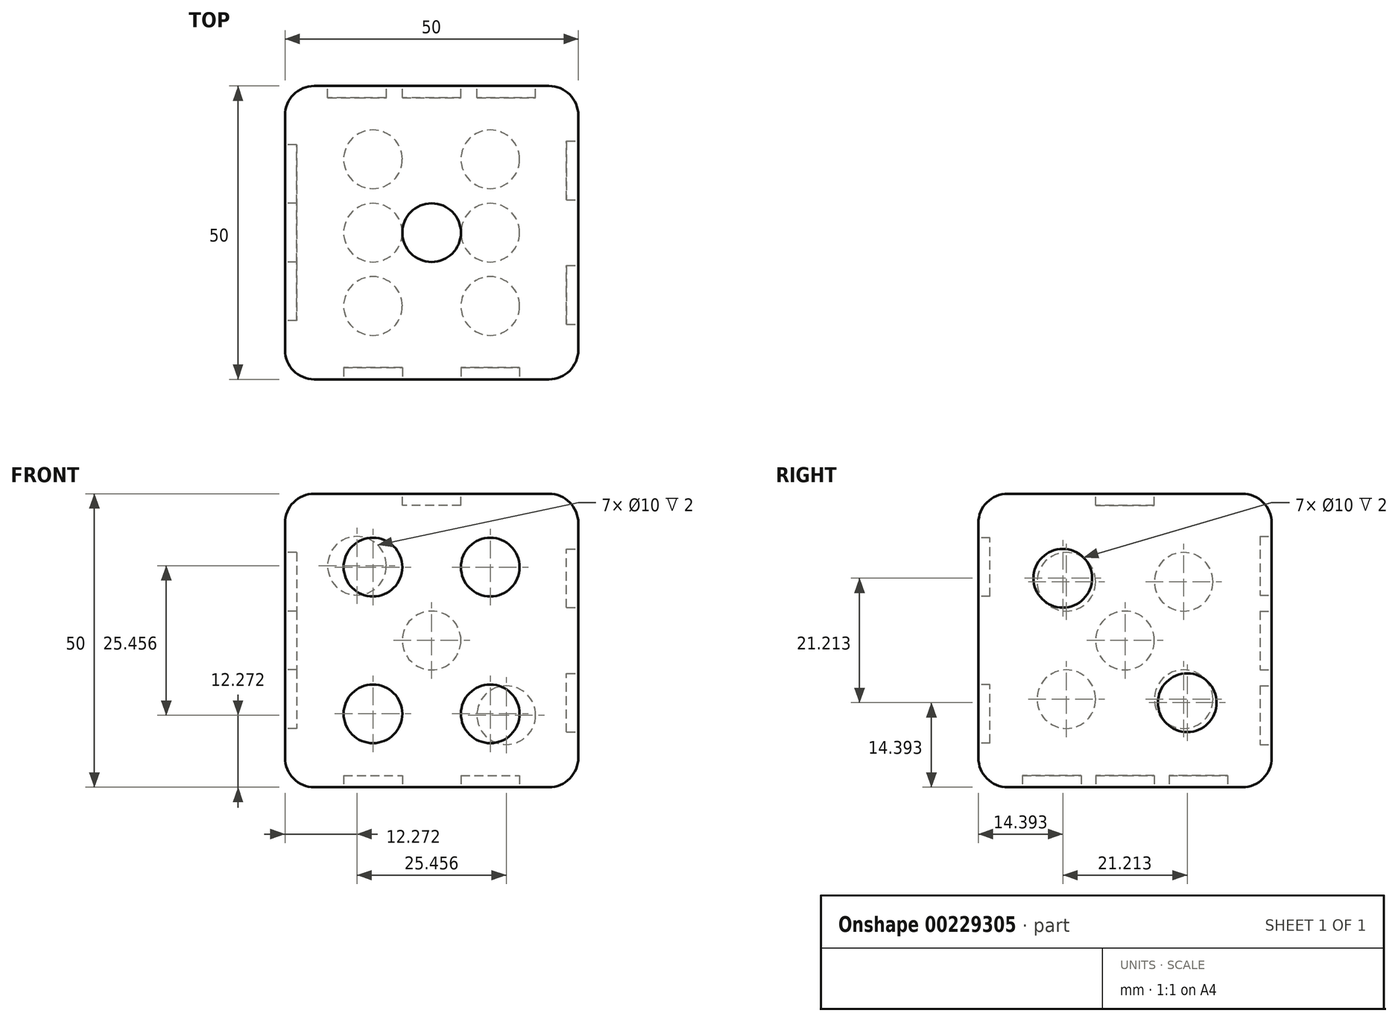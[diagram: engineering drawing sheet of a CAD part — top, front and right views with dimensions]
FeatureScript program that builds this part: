
annotation { "Feature Type Name" : "Feature", "Feature Type Description" : "" }
export const myFeature = defineFeature(function(context is Context, id is Id, definition is map)
    precondition{}
    {
        {
            var Q0;
            Q0=qCreatedBy(makeId("Top.planeOp"),FACE);
            var sketch = newSketch(context, id + "F0", { "sketchPlane" : qUnion([Q0])});
            skLineSegment(sketch, "E0.bottom", {"start": v(-25, 25) * mm, "end": v(25, 25) * mm});
            skLineSegment(sketch, "E0.top", {"start": v(-25, -25) * mm, "end": v(25, -25) * mm});
            skLineSegment(sketch, "E0.left", {"start": v(-25, 25) * mm, "end": v(-25, -25) * mm});
            skLineSegment(sketch, "E0.right", {"start": v(25, 25) * mm, "end": v(25, -25) * mm});
            skPoint(sketch, "E1", {"position": v(0, 25) * mm});
            skPoint(sketch, "E2", {"position": v(25, 0) * mm});
            skSolve(sketch);
        }
        {
            var Q0;
            Q0=makeQuery(id+"F0.imprint","IMPRINT",FACE,{"disambiguationData":[TD([[makeQuery(id+"F0.imprint","IMPRINT",EDGE,{"derivedFrom":sQuery(id+"F0.wireOp",EDGE,"E0.bottom")}),-1.0]])]});
            extrude(context, id + "F1", {"entities" : qUnion([Q0]), "depth" : 50 * mm});
        }
        {
            var Q0;
            Q0=makeQuery(id+"F1.opExtrude","CAP_FACE",FACE,{"disambiguationData":[OSD([sQuery(id+"F0.wireOp",EDGE,"E0.bottom"),sQuery(id+"F0.wireOp",EDGE,"E0.top"),sQuery(id+"F0.wireOp",EDGE,"E0.left"),sQuery(id+"F0.wireOp",EDGE,"E0.right")])],"isStart":false});
            var sketch = newSketch(context, id + "F2", { "sketchPlane" : qUnion([Q0])});
            skCircle(sketch, "E3", {"center": v(0, 0) * mm, "radius": 5 * mm});
            skSolve(sketch);
        }
        {
            var Q0;
            Q0=makeQuery(id+"F2.imprint","IMPRINT",FACE,{"disambiguationData":[TD([[makeQuery(id+"F2.imprint","IMPRINT",EDGE,{"derivedFrom":sQuery(id+"F2.wireOp",EDGE,"E3")}),1.0]])]});
            extrude(context, id + "F3", {"entities" : qUnion([Q0]), "operationType" : NewBodyOperationType.REMOVE, "oppositeDirection" : true, "depth" : 2 * mm});
        }
        {
            var Q0;
            Q0=makeQuery(id+"F1.opExtrude","SWEPT_FACE",FACE,{"disambiguationData":[OSD([sQuery(id+"F0.wireOp",EDGE,"E0.right")])]});
            var sketch = newSketch(context, id + "F4", { "sketchPlane" : qUnion([Q0])});
            skCircle(sketch, "E4", {"center": v(-10.6, 35.6) * mm, "radius": 5 * mm});
            skCircle(sketch, "E5", {"center": v(10.6, 14.4) * mm, "radius": 5 * mm});
            skLineSegment(sketch, "E6", {"start": v(-25, 50) * mm, "end": v(25, 0) * mm, "construction": true});
            skLineSegment(sketch, "E7", {"start": v(-10.6, 35.6) * mm, "end": v(10.6, 14.4) * mm, "construction": true});
            skPoint(sketch, "E8", {"position": v(0, 25) * mm});
            skSolve(sketch);
        }
        {
            var Q0;
            Q0=makeQuery(id+"F4.imprint","IMPRINT",FACE,{"disambiguationData":[TD([[makeQuery(id+"F4.imprint","IMPRINT",EDGE,{"derivedFrom":sQuery(id+"F4.wireOp",EDGE,"E5")}),1.0]])]});
            var Q1;
            Q1=makeQuery(id+"F4.imprint","IMPRINT",FACE,{"disambiguationData":[TD([[makeQuery(id+"F4.imprint","IMPRINT",EDGE,{"derivedFrom":sQuery(id+"F4.wireOp",EDGE,"E4")}),1.0]])]});
            var Q2;
            Q2=sQuery(id+"F4.wireOp",EDGE,"E4");
            var Q3;
            Q3=sQuery(id+"F4.wireOp",EDGE,"E5");
            extrude(context, id + "F5", {"entities" : qUnion([Q0, Q1]), "operationType" : NewBodyOperationType.REMOVE, "surfaceEntities" : qUnion([Q2, Q3]), "oppositeDirection" : true, "depth" : 2 * mm});
        }
        {
            var Q0;
            Q0=makeQuery(id+"F1.opExtrude","CAP_FACE",FACE,{"disambiguationData":[OSD([sQuery(id+"F0.wireOp",EDGE,"E0.bottom"),sQuery(id+"F0.wireOp",EDGE,"E0.top"),sQuery(id+"F0.wireOp",EDGE,"E0.left"),sQuery(id+"F0.wireOp",EDGE,"E0.right")])],"isStart":true});
            var sketch = newSketch(context, id + "F6", { "sketchPlane" : qUnion([Q0])});
            skCircle(sketch, "E9", {"center": v(10, 12.5) * mm, "radius": 5 * mm});
            skCircle(sketch, "E10", {"center": v(10, 0) * mm, "radius": 5 * mm});
            skCircle(sketch, "E11", {"center": v(10, -12.5) * mm, "radius": 5 * mm});
            skCircle(sketch, "E12", {"center": v(-10, 12.5) * mm, "radius": 5 * mm});
            skCircle(sketch, "E13", {"center": v(-10, 0) * mm, "radius": 5 * mm});
            skCircle(sketch, "E14", {"center": v(-10, -12.5) * mm, "radius": 5 * mm});
            skLineSegment(sketch, "E15", {"start": v(-10, 0) * mm, "end": v(10, 0) * mm, "construction": true});
            skPoint(sketch, "E16", {"position": v(0, 0) * mm});
            skLineSegment(sketch, "E17", {"start": v(-10, 12.5) * mm, "end": v(-10, -12.5) * mm, "construction": true});
            skLineSegment(sketch, "E18", {"start": v(10, 12.5) * mm, "end": v(10, -12.5) * mm, "construction": true});
            skSolve(sketch);
        }
        {
            var Q0;
            Q0=makeQuery(id+"F6.imprint","IMPRINT",FACE,{"disambiguationData":[TD([[makeQuery(id+"F6.imprint","IMPRINT",EDGE,{"derivedFrom":sQuery(id+"F6.wireOp",EDGE,"E11")}),1.0]])]});
            var Q1;
            Q1=makeQuery(id+"F6.imprint","IMPRINT",FACE,{"disambiguationData":[TD([[makeQuery(id+"F6.imprint","IMPRINT",EDGE,{"derivedFrom":sQuery(id+"F6.wireOp",EDGE,"E10")}),1.0]])]});
            var Q2;
            Q2=makeQuery(id+"F6.imprint","IMPRINT",FACE,{"disambiguationData":[TD([[makeQuery(id+"F6.imprint","IMPRINT",EDGE,{"derivedFrom":sQuery(id+"F6.wireOp",EDGE,"E9")}),1.0]])]});
            var Q3;
            Q3=makeQuery(id+"F6.imprint","IMPRINT",FACE,{"disambiguationData":[TD([[makeQuery(id+"F6.imprint","IMPRINT",EDGE,{"derivedFrom":sQuery(id+"F6.wireOp",EDGE,"E14")}),1.0]])]});
            var Q4;
            Q4=makeQuery(id+"F6.imprint","IMPRINT",FACE,{"disambiguationData":[TD([[makeQuery(id+"F6.imprint","IMPRINT",EDGE,{"derivedFrom":sQuery(id+"F6.wireOp",EDGE,"E13")}),1.0]])]});
            var Q5;
            Q5=makeQuery(id+"F6.imprint","IMPRINT",FACE,{"disambiguationData":[TD([[makeQuery(id+"F6.imprint","IMPRINT",EDGE,{"derivedFrom":sQuery(id+"F6.wireOp",EDGE,"E12")}),1.0]])]});
            extrude(context, id + "F7", {"entities" : qUnion([Q0, Q1, Q2, Q3, Q4, Q5]), "operationType" : NewBodyOperationType.REMOVE, "oppositeDirection" : true, "depth" : 2 * mm});
        }
        {
            var Q0;
            Q0=makeQuery(id+"F1.opExtrude","SWEPT_FACE",FACE,{"disambiguationData":[OSD([sQuery(id+"F0.wireOp",EDGE,"E0.bottom")])]});
            var sketch = newSketch(context, id + "F8", { "sketchPlane" : qUnion([Q0])});
            skLineSegment(sketch, "E19", {"start": v(25, 50) * mm, "end": v(-25, 0) * mm, "construction": true});
            skCircle(sketch, "E20", {"center": v(12.73, 37.73) * mm, "radius": 5 * mm});
            skCircle(sketch, "E21", {"center": v(-12.73, 12.27) * mm, "radius": 5 * mm});
            skPoint(sketch, "E22", {"position": v(0, 25) * mm});
            skCircle(sketch, "E23", {"center": v(0, 25) * mm, "radius": 5 * mm});
            skLineSegment(sketch, "E24", {"start": v(12.73, 37.73) * mm, "end": v(0, 25) * mm, "construction": true});
            skLineSegment(sketch, "E25", {"start": v(0, 25) * mm, "end": v(-12.73, 12.27) * mm, "construction": true});
            skSolve(sketch);
        }
        {
            var Q0;
            Q0=makeQuery(id+"F8.imprint","IMPRINT",FACE,{"disambiguationData":[TD([[makeQuery(id+"F8.imprint","IMPRINT",EDGE,{"derivedFrom":sQuery(id+"F8.wireOp",EDGE,"E21")}),1.0]])]});
            var Q1;
            Q1=makeQuery(id+"F8.imprint","IMPRINT",FACE,{"disambiguationData":[TD([[makeQuery(id+"F8.imprint","IMPRINT",EDGE,{"derivedFrom":sQuery(id+"F8.wireOp",EDGE,"E23")}),1.0]])]});
            var Q2;
            Q2=makeQuery(id+"F8.imprint","IMPRINT",FACE,{"disambiguationData":[TD([[makeQuery(id+"F8.imprint","IMPRINT",EDGE,{"derivedFrom":sQuery(id+"F8.wireOp",EDGE,"E20")}),1.0]])]});
            extrude(context, id + "F9", {"entities" : qUnion([Q0, Q1, Q2]), "operationType" : NewBodyOperationType.REMOVE, "oppositeDirection" : true, "depth" : 2 * mm});
        }
        {
            var Q0;
            Q0=makeQuery(id+"F1.opExtrude","SWEPT_FACE",FACE,{"disambiguationData":[OSD([sQuery(id+"F0.wireOp",EDGE,"E0.top")])]});
            var sketch = newSketch(context, id + "F10", { "sketchPlane" : qUnion([Q0])});
            skCircle(sketch, "E26", {"center": v(-10, 37.5) * mm, "radius": 5 * mm});
            skCircle(sketch, "E27", {"center": v(-10, 12.5) * mm, "radius": 5 * mm});
            skCircle(sketch, "E28", {"center": v(10, 12.5) * mm, "radius": 5 * mm});
            skCircle(sketch, "E29", {"center": v(10, 37.5) * mm, "radius": 5 * mm});
            skLineSegment(sketch, "E30", {"start": v(-10, 37.5) * mm, "end": v(10, 37.5) * mm, "construction": true});
            skLineSegment(sketch, "E31", {"start": v(-10, 12.5) * mm, "end": v(10, 12.5) * mm, "construction": true});
            skPoint(sketch, "E32", {"position": v(0, 37.5) * mm});
            skPoint(sketch, "E33", {"position": v(0, 12.5) * mm});
            skLineSegment(sketch, "E34", {"start": v(0, 37.5) * mm, "end": v(0, 12.5) * mm, "construction": true});
            skPoint(sketch, "E35", {"position": v(0, 25) * mm});
            skPoint(sketch, "E36", {"position": v(-25, 25) * mm});
            skPoint(sketch, "E37", {"position": v(25, 25) * mm});
            skLineSegment(sketch, "E38", {"start": v(-25, 25) * mm, "end": v(25, 25) * mm, "construction": true});
            skSolve(sketch);
        }
        {
            var Q0;
            Q0=makeQuery(id+"F10.imprint","IMPRINT",FACE,{"disambiguationData":[TD([[makeQuery(id+"F10.imprint","IMPRINT",EDGE,{"derivedFrom":sQuery(id+"F10.wireOp",EDGE,"E26")}),1.0]])]});
            var Q1;
            Q1=makeQuery(id+"F10.imprint","IMPRINT",FACE,{"disambiguationData":[TD([[makeQuery(id+"F10.imprint","IMPRINT",EDGE,{"derivedFrom":sQuery(id+"F10.wireOp",EDGE,"E27")}),1.0]])]});
            var Q2;
            Q2=makeQuery(id+"F10.imprint","IMPRINT",FACE,{"disambiguationData":[TD([[makeQuery(id+"F10.imprint","IMPRINT",EDGE,{"derivedFrom":sQuery(id+"F10.wireOp",EDGE,"E28")}),1.0]])]});
            var Q3;
            Q3=makeQuery(id+"F10.imprint","IMPRINT",FACE,{"disambiguationData":[TD([[makeQuery(id+"F10.imprint","IMPRINT",EDGE,{"derivedFrom":sQuery(id+"F10.wireOp",EDGE,"E29")}),1.0]])]});
            extrude(context, id + "F11", {"entities" : qUnion([Q0, Q1, Q2, Q3]), "operationType" : NewBodyOperationType.REMOVE, "oppositeDirection" : true, "depth" : 2 * mm});
        }
        {
            var Q0;
            Q0=makeQuery(id+"F1.opExtrude","SWEPT_FACE",FACE,{"disambiguationData":[OSD([sQuery(id+"F0.wireOp",EDGE,"E0.left")])]});
            var sketch = newSketch(context, id + "F12", { "sketchPlane" : qUnion([Q0])});
            skCircle(sketch, "E39", {"center": v(-10, 35) * mm, "radius": 5 * mm});
            skCircle(sketch, "E40", {"center": v(10, 35) * mm, "radius": 5 * mm});
            skCircle(sketch, "E41", {"center": v(-10, 15) * mm, "radius": 5 * mm});
            skCircle(sketch, "E42", {"center": v(10, 15) * mm, "radius": 5 * mm});
            skCircle(sketch, "E43", {"center": v(0, 25) * mm, "radius": 5 * mm});
            skLineSegment(sketch, "E44", {"start": v(-10, 35) * mm, "end": v(10, 35) * mm, "construction": true});
            skLineSegment(sketch, "E45", {"start": v(-10, 15) * mm, "end": v(10, 15) * mm, "construction": true});
            skPoint(sketch, "E46", {"position": v(0, 35) * mm});
            skPoint(sketch, "E47", {"position": v(0, 15) * mm});
            skPoint(sketch, "E48", {"position": v(0, 50) * mm});
            skPoint(sketch, "E49", {"position": v(-25, 25) * mm});
            skPoint(sketch, "E50", {"position": v(25, 25) * mm});
            skLineSegment(sketch, "E51", {"start": v(-25, 25) * mm, "end": v(25, 25) * mm, "construction": true});
            skLineSegment(sketch, "E52", {"start": v(0, 35) * mm, "end": v(0, 15) * mm, "construction": true});
            skSolve(sketch);
        }
        {
            var Q0;
            Q0=makeQuery(id+"F12.imprint","IMPRINT",FACE,{"disambiguationData":[TD([[makeQuery(id+"F12.imprint","IMPRINT",EDGE,{"derivedFrom":sQuery(id+"F12.wireOp",EDGE,"E39")}),1.0]])]});
            var Q1;
            Q1=makeQuery(id+"F12.imprint","IMPRINT",FACE,{"disambiguationData":[TD([[makeQuery(id+"F12.imprint","IMPRINT",EDGE,{"derivedFrom":sQuery(id+"F12.wireOp",EDGE,"E43")}),1.0]])]});
            var Q2;
            Q2=makeQuery(id+"F12.imprint","IMPRINT",FACE,{"disambiguationData":[TD([[makeQuery(id+"F12.imprint","IMPRINT",EDGE,{"derivedFrom":sQuery(id+"F12.wireOp",EDGE,"E40")}),1.0]])]});
            var Q3;
            Q3=makeQuery(id+"F12.imprint","IMPRINT",FACE,{"disambiguationData":[TD([[makeQuery(id+"F12.imprint","IMPRINT",EDGE,{"derivedFrom":sQuery(id+"F12.wireOp",EDGE,"E42")}),1.0]])]});
            var Q4;
            Q4=makeQuery(id+"F12.imprint","IMPRINT",FACE,{"disambiguationData":[TD([[makeQuery(id+"F12.imprint","IMPRINT",EDGE,{"derivedFrom":sQuery(id+"F12.wireOp",EDGE,"E41")}),1.0]])]});
            extrude(context, id + "F13", {"entities" : qUnion([Q0, Q1, Q2, Q3, Q4]), "operationType" : NewBodyOperationType.REMOVE, "oppositeDirection" : true, "depth" : 2 * mm});
        }
        {
            var Q0;
            Q0=makeQuery(id+"F1.opExtrude","CAP_EDGE",EDGE,{"disambiguationData":[OSD([sQuery(id+"F0.wireOp",EDGE,"E0.right")])],"isStart":false});
            var Q1;
            Q1=makeQuery(id+"F1.opExtrude","SWEPT_EDGE",EDGE,{"disambiguationData":[OSD([sQuery(id+"F0.wireOp",EDGE,"E0.top"),sQuery(id+"F0.wireOp",EDGE,"E0.right")])]});
            var Q2;
            Q2=makeQuery(id+"F1.opExtrude","SWEPT_EDGE",EDGE,{"disambiguationData":[OSD([sQuery(id+"F0.wireOp",EDGE,"E0.top"),sQuery(id+"F0.wireOp",EDGE,"E0.left")])]});
            var Q3;
            Q3=makeQuery(id+"F1.opExtrude","CAP_EDGE",EDGE,{"disambiguationData":[OSD([sQuery(id+"F0.wireOp",EDGE,"E0.bottom")])],"isStart":true});
            var Q4;
            Q4=makeQuery(id+"F1.opExtrude","SWEPT_EDGE",EDGE,{"disambiguationData":[OSD([sQuery(id+"F0.wireOp",EDGE,"E0.bottom"),sQuery(id+"F0.wireOp",EDGE,"E0.left")])]});
            var Q5;
            Q5=makeQuery(id+"F1.opExtrude","CAP_EDGE",EDGE,{"disambiguationData":[OSD([sQuery(id+"F0.wireOp",EDGE,"E0.left")])],"isStart":false});
            var Q6;
            Q6=makeQuery(id+"F1.opExtrude","CAP_EDGE",EDGE,{"disambiguationData":[OSD([sQuery(id+"F0.wireOp",EDGE,"E0.right")])],"isStart":true});
            var Q7;
            Q7=makeQuery(id+"F1.opExtrude","CAP_EDGE",EDGE,{"disambiguationData":[OSD([sQuery(id+"F0.wireOp",EDGE,"E0.top")])],"isStart":true});
            var Q8;
            Q8=makeQuery(id+"F1.opExtrude","SWEPT_EDGE",EDGE,{"disambiguationData":[OSD([sQuery(id+"F0.wireOp",EDGE,"E0.bottom"),sQuery(id+"F0.wireOp",EDGE,"E0.right")])]});
            var Q9;
            Q9=makeQuery(id+"F1.opExtrude","CAP_EDGE",EDGE,{"disambiguationData":[OSD([sQuery(id+"F0.wireOp",EDGE,"E0.left")])],"isStart":true});
            var Q10;
            Q10=makeQuery(id+"F1.opExtrude","CAP_EDGE",EDGE,{"disambiguationData":[OSD([sQuery(id+"F0.wireOp",EDGE,"E0.bottom")])],"isStart":false});
            var Q11;
            Q11=makeQuery(id+"F1.opExtrude","CAP_EDGE",EDGE,{"disambiguationData":[OSD([sQuery(id+"F0.wireOp",EDGE,"E0.top")])],"isStart":false});
            fillet(context, id + "F14", {"entities" : qUnion([Q0, Q1, Q2, Q3, Q4, Q5, Q6, Q7, Q8, Q9, Q10, Q11]), "radius" : 5 * mm, "tangentPropagation" : true, "allowEdgeOverflow" : false});
        }
    });
